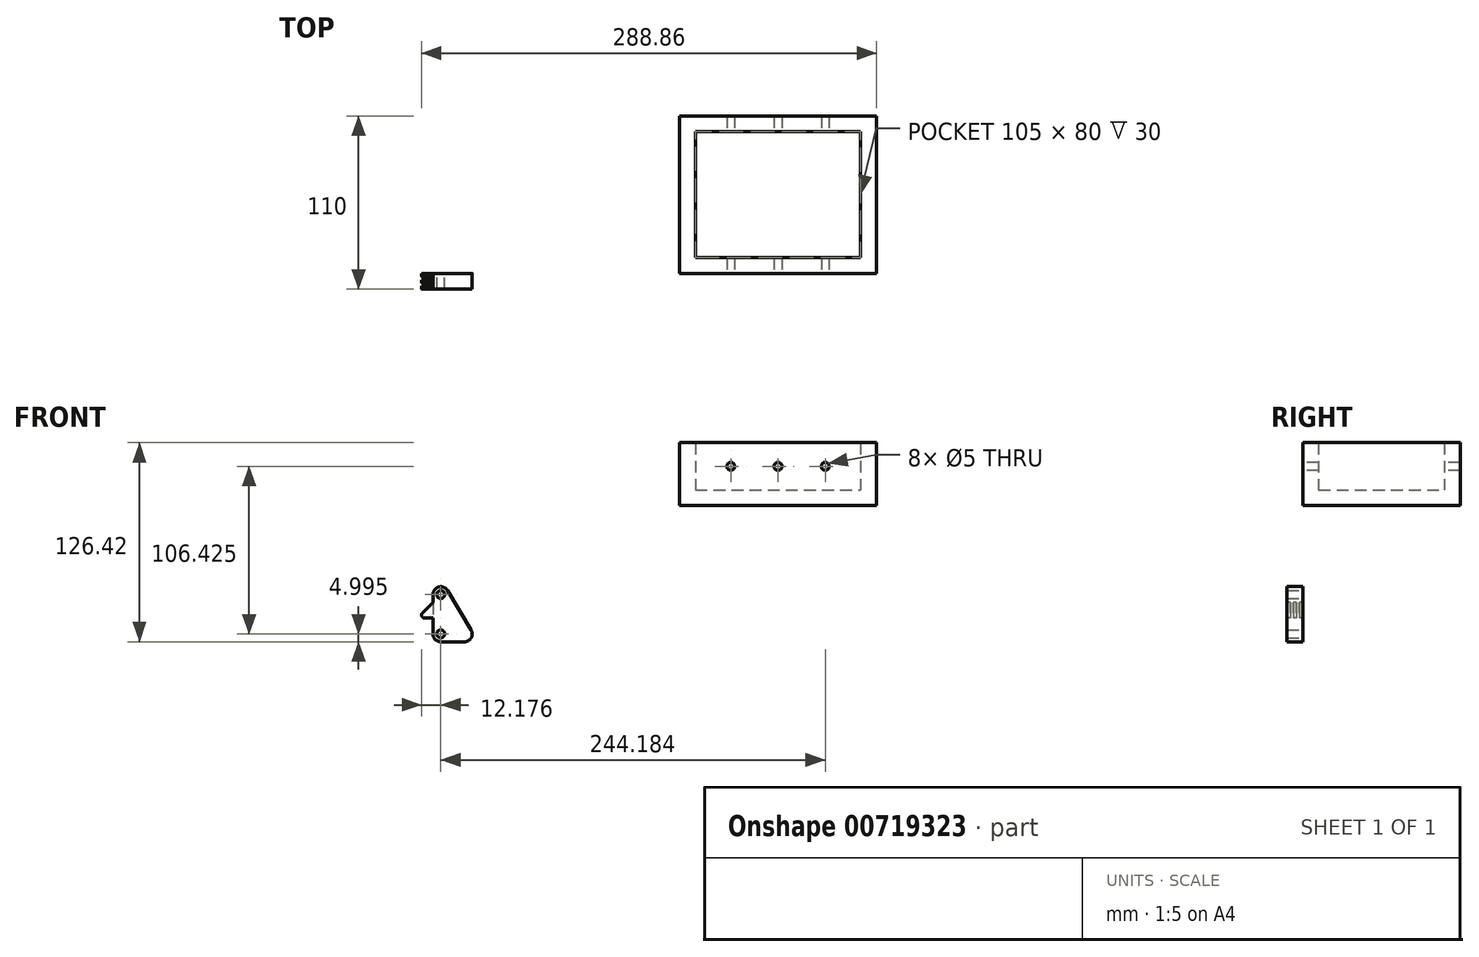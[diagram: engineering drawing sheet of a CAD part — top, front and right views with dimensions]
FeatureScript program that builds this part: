
annotation { "Feature Type Name" : "Feature", "Feature Type Description" : "" }
export const myFeature = defineFeature(function(context is Context, id is Id, definition is map)
    precondition{}
    {
        {
            var Q0;
            Q0=qCreatedBy(makeId("Top.planeOp"),FACE);
            var sketch = newSketch(context, id + "F0", { "sketchPlane" : qUnion([Q0])});
            skLineSegment(sketch, "E0.bottom", {"start": v(0, 0) * mm, "end": v(125, 0) * mm});
            skLineSegment(sketch, "E0.top", {"start": v(0, 100) * mm, "end": v(125, 100) * mm});
            skLineSegment(sketch, "E0.left", {"start": v(0, 0) * mm, "end": v(0, 100) * mm});
            skLineSegment(sketch, "E0.right", {"start": v(125, 0) * mm, "end": v(125, 100) * mm});
            skLineSegment(sketch, "E1.bottom", {"start": v(10, 10) * mm, "end": v(115, 10) * mm});
            skLineSegment(sketch, "E1.top", {"start": v(10, 90) * mm, "end": v(115, 90) * mm});
            skLineSegment(sketch, "E1.left", {"start": v(10, 10) * mm, "end": v(10, 90) * mm});
            skLineSegment(sketch, "E1.right", {"start": v(115, 10) * mm, "end": v(115, 90) * mm});
            skSolve(sketch);
        }
        {
            var Q0;
            Q0=makeQuery(id+"F0.imprint","IMPRINT",FACE,{"disambiguationData":[TD([[makeQuery(id+"F0.imprint","IMPRINT",EDGE,{"derivedFrom":sQuery(id+"F0.wireOp",EDGE,"E0.bottom")}),1.0]])]});
            extrude(context, id + "F1", {"entities" : qUnion([Q0]), "depth" : 30 * mm, "offsetDistance" : 25 * mm});
        }
        {
            var Q0;
            Q0=makeQuery(id+"F1.opExtrude","SWEPT_FACE",FACE,{"disambiguationData":[OSD([sQuery(id+"F0.wireOp",EDGE,"E0.bottom")])]});
            var sketch = newSketch(context, id + "F2", { "sketchPlane" : qUnion([Q0])});
            skCircle(sketch, "E2", {"center": v(62.5, 15) * mm, "radius": 2.5 * mm});
            skCircle(sketch, "E3", {"center": v(92.5, 15) * mm, "radius": 2.5 * mm});
            skCircle(sketch, "E4", {"center": v(32.5, 15) * mm, "radius": 2.5 * mm});
            skSolve(sketch);
        }
        {
            var Q0;
            Q0=makeQuery(id+"F2.imprint","IMPRINT",FACE,{"disambiguationData":[TD([[makeQuery(id+"F2.imprint","IMPRINT",EDGE,{"derivedFrom":sQuery(id+"F2.wireOp",EDGE,"E4")}),1.0]])]});
            var Q1;
            Q1=makeQuery(id+"F2.imprint","IMPRINT",FACE,{"disambiguationData":[TD([[makeQuery(id+"F2.imprint","IMPRINT",EDGE,{"derivedFrom":sQuery(id+"F2.wireOp",EDGE,"E2")}),1.0]])]});
            var Q2;
            Q2=makeQuery(id+"F2.imprint","IMPRINT",FACE,{"disambiguationData":[TD([[makeQuery(id+"F2.imprint","IMPRINT",EDGE,{"derivedFrom":sQuery(id+"F2.wireOp",EDGE,"E3")}),1.0]])]});
            extrude(context, id + "F3", {"entities" : qUnion([Q0, Q1, Q2]), "operationType" : NewBodyOperationType.REMOVE, "endBound" : BoundingType.THROUGH_ALL, "oppositeDirection" : true, "depth" : 25 * mm, "offsetDistance" : 25 * mm});
        }
        {
            var Q0;
            Q0=makeQuery(id+"F1.opExtrude","CAP_FACE",FACE,{"disambiguationData":[OSD([sQuery(id+"F0.wireOp",EDGE,"E0.bottom"),sQuery(id+"F0.wireOp",EDGE,"E0.top"),sQuery(id+"F0.wireOp",EDGE,"E0.left"),sQuery(id+"F0.wireOp",EDGE,"E0.right"),sQuery(id+"F0.wireOp",EDGE,"E1.bottom"),sQuery(id+"F0.wireOp",EDGE,"E1.top"),sQuery(id+"F0.wireOp",EDGE,"E1.left"),sQuery(id+"F0.wireOp",EDGE,"E1.right")])],"isStart":true});
            var sketch = newSketch(context, id + "F4", { "sketchPlane" : qUnion([Q0])});
            skLineSegment(sketch, "E5.bottom", {"start": v(0, 0) * mm, "end": v(125, 0) * mm});
            skLineSegment(sketch, "E5.top", {"start": v(0, -100) * mm, "end": v(125, -100) * mm});
            skLineSegment(sketch, "E5.left", {"start": v(0, 0) * mm, "end": v(0, -100) * mm});
            skLineSegment(sketch, "E5.right", {"start": v(125, 0) * mm, "end": v(125, -100) * mm});
            skSolve(sketch);
        }
        {
            var Q0;
            Q0=makeQuery(id+"F4.imprint","IMPRINT",FACE,{"disambiguationData":[TD([[makeQuery(id+"F4.imprint","IMPRINT",EDGE,{"derivedFrom":sQuery(id+"F4.wireOp",EDGE,"E5.bottom")}),-1.0]])]});
            var Q1;
            Q1=makeQuery(id+"F4.imprint","IMPRINT",FACE,{"disambiguationData":[TD([[makeQuery(id+"F4.imprint","IMPRINT",EDGE,{"derivedFrom":makeQuery(id+"F1.opExtrude","CAP_EDGE",EDGE,{"disambiguationData":[OSD([sQuery(id+"F0.wireOp",EDGE,"E1.bottom")])],"isStart":true})}),-1.0]])]});
            extrude(context, id + "F5", {"entities" : qUnion([Q0, Q1]), "operationType" : NewBodyOperationType.ADD, "depth" : 10 * mm, "offsetDistance" : 25 * mm});
        }
        {
            var Q0;
            Q0=qCreatedBy(makeId("Right.planeOp"),FACE);
            cPlane(context, id + "F6", {"entities" : qUnion([Q0]), "cplaneType" : CPlaneType.OFFSET, "offset" : 60 * mm, "width" : 150 * mm, "height" : 150 * mm});
        }
        {
            var Q0;
            Q0=qCreatedBy(makeId("Front.planeOp"),FACE);
            var sketch = newSketch(context, id + "F7", { "sketchPlane" : qUnion([Q0])});
            skLineSegment(sketch, "E6", {"start": v(-156.68, -66.42) * mm, "end": v(-156.68, -91.42) * mm});
            skArc(sketch, "E7", {"start": v(-156.68, -91.42) * mm, "mid": v(-155.22, -94.96) * mm, "end": v(-151.68, -96.42) * mm});
            skLineSegment(sketch, "E8", {"start": v(-151.68, -96.42) * mm, "end": v(-136.68, -96.42) * mm});
            skArc(sketch, "E9", {"start": v(-136.68, -96.42) * mm, "mid": v(-132.33, -93.89) * mm, "end": v(-132.4, -88.85) * mm});
            skArc(sketch, "E10", {"start": v(-147.4, -63.85) * mm, "mid": v(-153.02, -61.6) * mm, "end": v(-156.68, -66.42) * mm});
            skLineSegment(sketch, "E11", {"start": v(-132.4, -88.85) * mm, "end": v(-147.4, -63.85) * mm});
            skCircle(sketch, "E12", {"center": v(-151.68, -66.42) * mm, "radius": 2.5 * mm});
            skCircle(sketch, "E13", {"center": v(-151.68, -91.42) * mm, "radius": 2.5 * mm});
            skSolve(sketch);
        }
        {
            var Q0;
            Q0=makeQuery(id+"F7.imprint","IMPRINT",FACE,{"disambiguationData":[TD([[makeQuery(id+"F7.imprint","IMPRINT",EDGE,{"derivedFrom":sQuery(id+"F7.wireOp",EDGE,"E6")}),1.0]])]});
            extrude(context, id + "F8", {"entities" : qUnion([Q0]), "depth" : 10 * mm, "offsetDistance" : 25 * mm});
        }
        {
            var Q0;
            Q0=makeQuery(id+"F8.opExtrude","CAP_FACE",FACE,{"disambiguationData":[OSD([sQuery(id+"F7.wireOp",EDGE,"E6"),sQuery(id+"F7.wireOp",EDGE,"E7"),sQuery(id+"F7.wireOp",EDGE,"E8"),sQuery(id+"F7.wireOp",EDGE,"E9"),sQuery(id+"F7.wireOp",EDGE,"E10"),sQuery(id+"F7.wireOp",EDGE,"E11"),sQuery(id+"F7.wireOp",EDGE,"E12"),sQuery(id+"F7.wireOp",EDGE,"E13")])],"isStart":false});
            var sketch = newSketch(context, id + "F9", { "sketchPlane" : qUnion([Q0])});
            skLineSegment(sketch, "E14", {"start": v(-156.68, -71.42) * mm, "end": v(-163.27, -78.01) * mm});
            skLineSegment(sketch, "E15", {"start": v(-161.86, -81.42) * mm, "end": v(-156.68, -81.42) * mm});
            skPoint(sketch, "E16.visualSharp", {"position": v(-166.68, -81.42) * mm});
            skArc(sketch, "E16.filletArc", {"start": v(-163.27, -78.01) * mm, "mid": v(-163.7, -80.2) * mm, "end": v(-161.86, -81.42) * mm});
            skSolve(sketch);
        }
        {
            var Q0;
            {var subQ0=sQuery(id+"F9.wireOp",EDGE,"E14");Q0=makeQuery(id+"F9.imprint","IMPRINT",FACE,{"disambiguationData":[TD([[makeQuery(id+"F9.imprint","IMPRINT",EDGE,{"derivedFrom":subQ0}),1.0]])]});}
            extrude(context, id + "F10", {"entities" : qUnion([Q0]), "operationType" : NewBodyOperationType.ADD, "oppositeDirection" : true, "depth" : 10 * mm, "offsetDistance" : 25 * mm});
        }
        {
            var Q0;
            Q0=makeQuery(id+"F10.opExtrude","SWEPT_FACE",FACE,{"disambiguationData":[OSD([sQuery(id+"F9.wireOp",EDGE,"E15")])]});
            var sketch = newSketch(context, id + "F11", { "sketchPlane" : qUnion([Q0])});
            skLineSegment(sketch, "E17.bottom", {"start": v(-156.68, 2) * mm, "end": v(-173.13, 2) * mm});
            skLineSegment(sketch, "E17.top", {"start": v(-156.68, 4) * mm, "end": v(-173.13, 4) * mm});
            skLineSegment(sketch, "E17.left", {"start": v(-156.68, 2) * mm, "end": v(-156.68, 4) * mm});
            skLineSegment(sketch, "E17.right", {"start": v(-173.13, 2) * mm, "end": v(-173.13, 4) * mm});
            skLineSegment(sketch, "E18.bottom", {"start": v(-156.68, 6) * mm, "end": v(-173.76, 6) * mm});
            skLineSegment(sketch, "E18.top", {"start": v(-156.68, 8) * mm, "end": v(-173.76, 8) * mm});
            skLineSegment(sketch, "E18.left", {"start": v(-156.68, 6) * mm, "end": v(-156.68, 8) * mm});
            skLineSegment(sketch, "E18.right", {"start": v(-173.76, 6) * mm, "end": v(-173.76, 8) * mm});
            skSolve(sketch);
        }
        {
            var Q0;
            {var subQ0=sQuery(id+"F11.wireOp",EDGE,"E18.right");Q0=makeQuery(id+"F11.imprint","IMPRINT",FACE,{"disambiguationData":[TD([[makeQuery(id+"F11.imprint","IMPRINT",EDGE,{"derivedFrom":subQ0}),-1.0]])]});}
            var Q1;
            {var subQ0=sQuery(id+"F11.wireOp",EDGE,"E17.left");Q1=makeQuery(id+"F11.imprint","IMPRINT",FACE,{"disambiguationData":[TD([[makeQuery(id+"F11.imprint","IMPRINT",EDGE,{"derivedFrom":subQ0}),1.0]])]});}
            var Q2;
            {var subQ0=sQuery(id+"F11.wireOp",EDGE,"E18.left");Q2=makeQuery(id+"F11.imprint","IMPRINT",FACE,{"disambiguationData":[TD([[makeQuery(id+"F11.imprint","IMPRINT",EDGE,{"derivedFrom":subQ0}),1.0]])]});}
            var Q3;
            {var subQ0=sQuery(id+"F11.wireOp",EDGE,"E17.right");Q3=makeQuery(id+"F11.imprint","IMPRINT",FACE,{"disambiguationData":[TD([[makeQuery(id+"F11.imprint","IMPRINT",EDGE,{"derivedFrom":subQ0}),-1.0]])]});}
            extrude(context, id + "F12", {"entities" : qUnion([Q0, Q1, Q2, Q3]), "operationType" : NewBodyOperationType.REMOVE, "oppositeDirection" : true, "depth" : 25 * mm, "offsetDistance" : 25 * mm});
        }
    });
